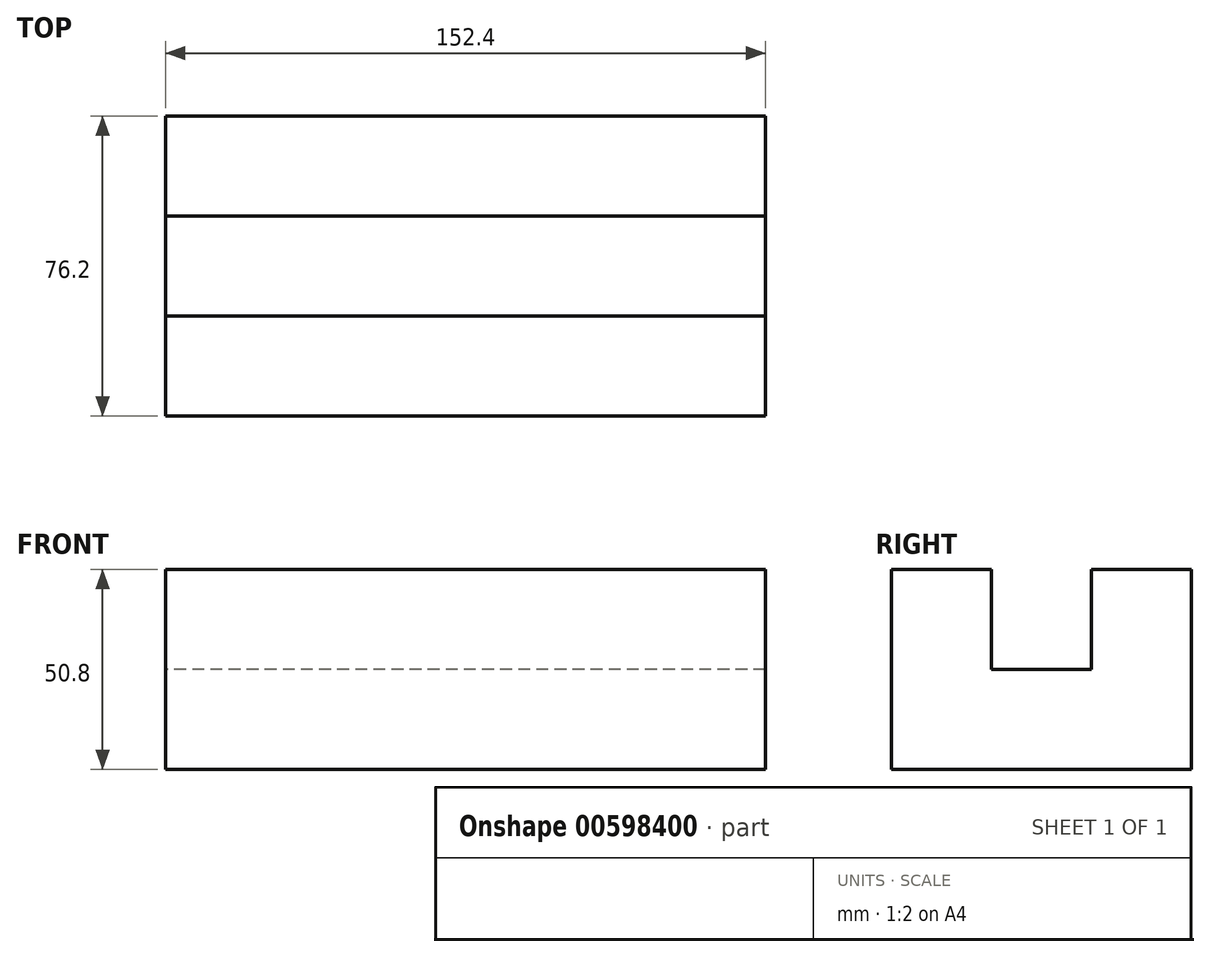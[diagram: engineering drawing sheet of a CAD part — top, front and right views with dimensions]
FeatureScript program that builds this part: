
annotation { "Feature Type Name" : "Feature", "Feature Type Description" : "" }
export const myFeature = defineFeature(function(context is Context, id is Id, definition is map)
    precondition{}
    {
        {
            var Q0;
            Q0=qCreatedBy(makeId("Right.planeOp"),FACE);
            var sketch = newSketch(context, id + "F0", { "sketchPlane" : qUnion([Q0])});
            skLineSegment(sketch, "E0", {"start": v(0, 0) * mm, "end": v(0, 50.8) * mm});
            skLineSegment(sketch, "E1", {"start": v(0, 50.8) * mm, "end": v(25.4, 50.8) * mm});
            skLineSegment(sketch, "E2", {"start": v(25.4, 50.8) * mm, "end": v(25.4, 25.4) * mm});
            skLineSegment(sketch, "E3", {"start": v(25.4, 25.4) * mm, "end": v(50.8, 25.4) * mm});
            skLineSegment(sketch, "E4", {"start": v(50.8, 25.4) * mm, "end": v(50.8, 50.8) * mm});
            skLineSegment(sketch, "E5", {"start": v(50.8, 50.8) * mm, "end": v(76.2, 50.8) * mm});
            skLineSegment(sketch, "E6", {"start": v(76.2, 50.8) * mm, "end": v(76.2, 0) * mm});
            skLineSegment(sketch, "E7", {"start": v(76.2, 0) * mm, "end": v(0, 0) * mm});
            skSolve(sketch);
        }
        {
            var Q0;
            Q0 = qSketchRegion(id + "F0", true);
            extrude(context, id + "F1", {"entities" : qUnion([Q0]), "depth" : 152.4 * mm, "offsetDistance" : 25.4 * mm});
        }
    });
